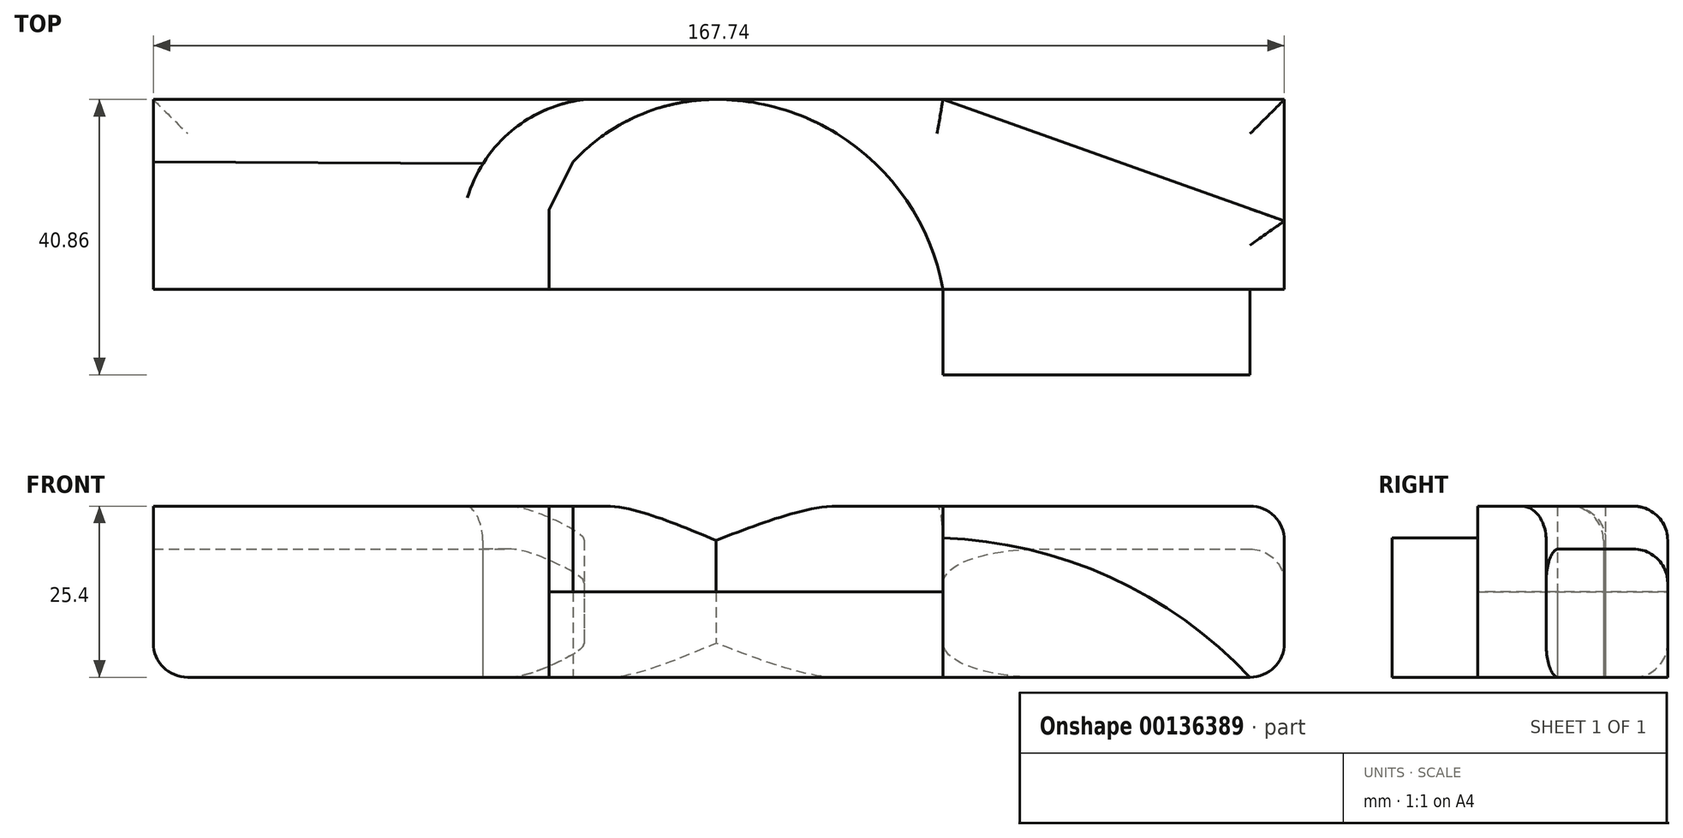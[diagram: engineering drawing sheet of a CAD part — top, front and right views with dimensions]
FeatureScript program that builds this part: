
annotation { "Feature Type Name" : "Feature", "Feature Type Description" : "" }
export const myFeature = defineFeature(function(context is Context, id is Id, definition is map)
    precondition{}
    {
        {
            var Q0;
            Q0=qCreatedBy(makeId("Top.planeOp"),FACE);
            var sketch = newSketch(context, id + "F0", { "sketchPlane" : qUnion([Q0])});
            skLineSegment(sketch, "E0.right", {"start": v(-62.28, 0) * mm, "end": v(-62.28, 18.92) * mm});
            skLineSegment(sketch, "E1", {"start": v(-62.28, 18.92) * mm, "end": v(-62.28, 28.16) * mm});
            skLineSegment(sketch, "E2", {"start": v(-62.28, 28.16) * mm, "end": v(21.16, 28.16) * mm});
            skArc(sketch, "E3", {"start": v(6.56, 28.16) * mm, "mid": v(-4.8, 26.29) * mm, "end": v(-13.4, 18.62) * mm});
            skLineSegment(sketch, "E4", {"start": v(-62.28, 18.92) * mm, "end": v(-13.4, 18.62) * mm});
            skLineSegment(sketch, "E5", {"start": v(21.16, 28.16) * mm, "end": v(54.83, 28.16) * mm});
            skLineSegment(sketch, "E6", {"start": v(54.83, 28.16) * mm, "end": v(105.46, 10.13) * mm});
            skLineSegment(sketch, "E7", {"start": v(105.46, 10.13) * mm, "end": v(105.46, 0) * mm});
            skLineSegment(sketch, "E8", {"start": v(105.46, 0) * mm, "end": v(54.83, 0) * mm});
            skArc(sketch, "E9", {"start": v(54.83, 0) * mm, "mid": v(43.1, 20.2) * mm, "end": v(21.16, 28.16) * mm});
            skArc(sketch, "E10", {"start": v(21.16, 28.16) * mm, "mid": v(9.61, 25.75) * mm, "end": v(0, 18.92) * mm});
            skLineSegment(sketch, "E11", {"start": v(0, 18.92) * mm, "end": v(-3.58, 11.77) * mm});
            skLineSegment(sketch, "E12", {"start": v(-3.58, 11.77) * mm, "end": v(-3.58, 0) * mm});
            skLineSegment(sketch, "E13", {"start": v(-3.58, 0) * mm, "end": v(-62.28, 0) * mm});
            skLineSegment(sketch, "E14", {"start": v(-3.58, 0) * mm, "end": v(54.83, 0) * mm});
            skLineSegment(sketch, "E15", {"start": v(54.83, 28.16) * mm, "end": v(105.46, 28.16) * mm});
            skLineSegment(sketch, "E16", {"start": v(105.46, 28.16) * mm, "end": v(105.46, 10.13) * mm});
            skSolve(sketch);
        }
        {
            var Q0;
            Q0=makeQuery(id+"F0.imprint","IMPRINT",FACE,{"disambiguationData":[TD([[makeQuery(id+"F0.imprint","IMPRINT",EDGE,{"derivedFrom":sQuery(id+"F0.wireOp",EDGE,"E0.right")}),-1.0]])]});
            var Q1;
            Q1=makeQuery(id+"F0.imprint","IMPRINT",FACE,{"disambiguationData":[TD([[makeQuery(id+"F0.imprint","IMPRINT",EDGE,{"derivedFrom":sQuery(id+"F0.wireOp",EDGE,"E5")}),-1.0]])]});
            extrude(context, id + "F1", {"entities" : qUnion([Q0, Q1]), "depth" : 25.4 * mm});
        }
        {
            var Q0;
            {var subQ0=sQuery(id+"F0.wireOp",EDGE,"E1");Q0=makeQuery(id+"F0.imprint","IMPRINT",FACE,{"disambiguationData":[TD([[makeQuery(id+"F0.imprint","IMPRINT",EDGE,{"derivedFrom":subQ0}),-1.0]])]});}
            var Q1;
            Q1=makeQuery(id+"F0.imprint","IMPRINT",FACE,{"disambiguationData":[TD([[makeQuery(id+"F0.imprint","IMPRINT",EDGE,{"derivedFrom":sQuery(id+"F0.wireOp",EDGE,"E6")}),1.0]])]});
            extrude(context, id + "F2", {"entities" : qUnion([Q0, Q1]), "depth" : 19.05 * mm});
        }
        {
            var Q0;
            Q0=makeQuery(id+"F0.imprint","IMPRINT",FACE,{"disambiguationData":[TD([[makeQuery(id+"F0.imprint","IMPRINT",EDGE,{"derivedFrom":sQuery(id+"F0.wireOp",EDGE,"E9")}),1.0]])]});
            extrude(context, id + "F3", {"entities" : qUnion([Q0]), "depth" : 12.7 * mm});
        }
        {
            var Q0;
            Q0=makeQuery(id+"F1.opExtrude","CAP_EDGE",EDGE,{"disambiguationData":[OSD([sQuery(id+"F0.wireOp",EDGE,"E6")])],"isStart":false});
            var Q1;
            Q1=makeQuery(id+"F2.opExtrude","CAP_EDGE",EDGE,{"disambiguationData":[OSD([sQuery(id+"F0.wireOp",EDGE,"E15")])],"isStart":false});
            var Q2;
            Q2=makeQuery(id+"F2.opExtrude","CAP_EDGE",EDGE,{"disambiguationData":[OSD([sQuery(id+"F0.wireOp",EDGE,"E16")])],"isStart":false});
            var Q3;
            Q3=makeQuery(id+"F1.opExtrude","CAP_EDGE",EDGE,{"disambiguationData":[OSD([sQuery(id+"F0.wireOp",EDGE,"E4")])],"isStart":false});
            var Q4;
            Q4=makeQuery(id+"F2.opExtrude","CAP_EDGE",EDGE,{"disambiguationData":[OSD([sQuery(id+"F0.wireOp",EDGE,"E2")])],"isStart":false});
            var Q5;
            Q5=makeQuery(id+"F1.opExtrude","CAP_EDGE",EDGE,{"disambiguationData":[OSD([sQuery(id+"F0.wireOp",EDGE,"E7")])],"isStart":false});
            var Q6;
            Q6=makeQuery(id+"F1.opExtrude","CAP_EDGE",EDGE,{"disambiguationData":[OSD([sQuery(id+"F0.wireOp",EDGE,"E5")])],"isStart":false});
            var Q7;
            Q7=makeQuery(id+"F1.opExtrude","CAP_EDGE",EDGE,{"disambiguationData":[OSD([sQuery(id+"F0.wireOp",EDGE,"E2")])],"isStart":false});
            fillet(context, id + "F4", {"entities" : qUnion([Q0, Q1, Q2, Q3, Q4, Q5, Q6, Q7]), "radius" : 5.08 * mm, "tangentPropagation" : true, "allowEdgeOverflow" : false});
        }
        {
            var Q0;
            Q0=makeQuery(id+"F1.opExtrude","CAP_EDGE",EDGE,{"disambiguationData":[OSD([sQuery(id+"F0.wireOp",EDGE,"E7")])],"isStart":true});
            var Q1;
            Q1=makeQuery(id+"F2.opExtrude","CAP_EDGE",EDGE,{"disambiguationData":[OSD([sQuery(id+"F0.wireOp",EDGE,"E16")])],"isStart":true});
            var Q2;
            Q2=makeQuery(id+"F1.opExtrude","CAP_EDGE",EDGE,{"disambiguationData":[OSD([sQuery(id+"F0.wireOp",EDGE,"E5")])],"isStart":true});
            var Q3;
            Q3=makeQuery(id+"F1.opExtrude","CAP_EDGE",EDGE,{"disambiguationData":[OSD([sQuery(id+"F0.wireOp",EDGE,"E2")])],"isStart":true});
            var Q4;
            Q4=makeQuery(id+"F2.opExtrude","CAP_EDGE",EDGE,{"disambiguationData":[OSD([sQuery(id+"F0.wireOp",EDGE,"E2")])],"isStart":true});
            var Q5;
            Q5=makeQuery(id+"F2.opExtrude","CAP_EDGE",EDGE,{"disambiguationData":[OSD([sQuery(id+"F0.wireOp",EDGE,"E1")])],"isStart":true});
            var Q6;
            Q6=makeQuery(id+"F1.opExtrude","CAP_EDGE",EDGE,{"disambiguationData":[OSD([sQuery(id+"F0.wireOp",EDGE,"E0.right")])],"isStart":true});
            fillet(context, id + "F5", {"entities" : qUnion([Q0, Q1, Q2, Q3, Q4, Q5, Q6]), "radius" : 5.08 * mm, "tangentPropagation" : true, "allowEdgeOverflow" : false});
        }
        {
            var Q0;
            Q0=makeQuery(id+"F1.opExtrude","SWEPT_FACE",FACE,{"disambiguationData":[OSD([sQuery(id+"F0.wireOp",EDGE,"E8")])]});
            var sketch = newSketch(context, id + "F6", { "sketchPlane" : qUnion([Q0])});
            skArc(sketch, "E17", {"start": v(100.38, 0) * mm, "mid": v(79.64, 14.84) * mm, "end": v(54.83, 20.71) * mm});
            skSolve(sketch);
        }
        {
            var Q0;
            {var subQ0=sQuery(id+"F6.wireOp",EDGE,"E17");Q0=makeQuery(id+"F6.imprint","IMPRINT",FACE,{"disambiguationData":[TD([[makeQuery(id+"F6.imprint","IMPRINT",EDGE,{"derivedFrom":subQ0}),1.0]])]});}
            extrude(context, id + "F7", {"entities" : qUnion([Q0]), "operationType" : NewBodyOperationType.ADD, "depth" : 12.7 * mm});
        }
    });
